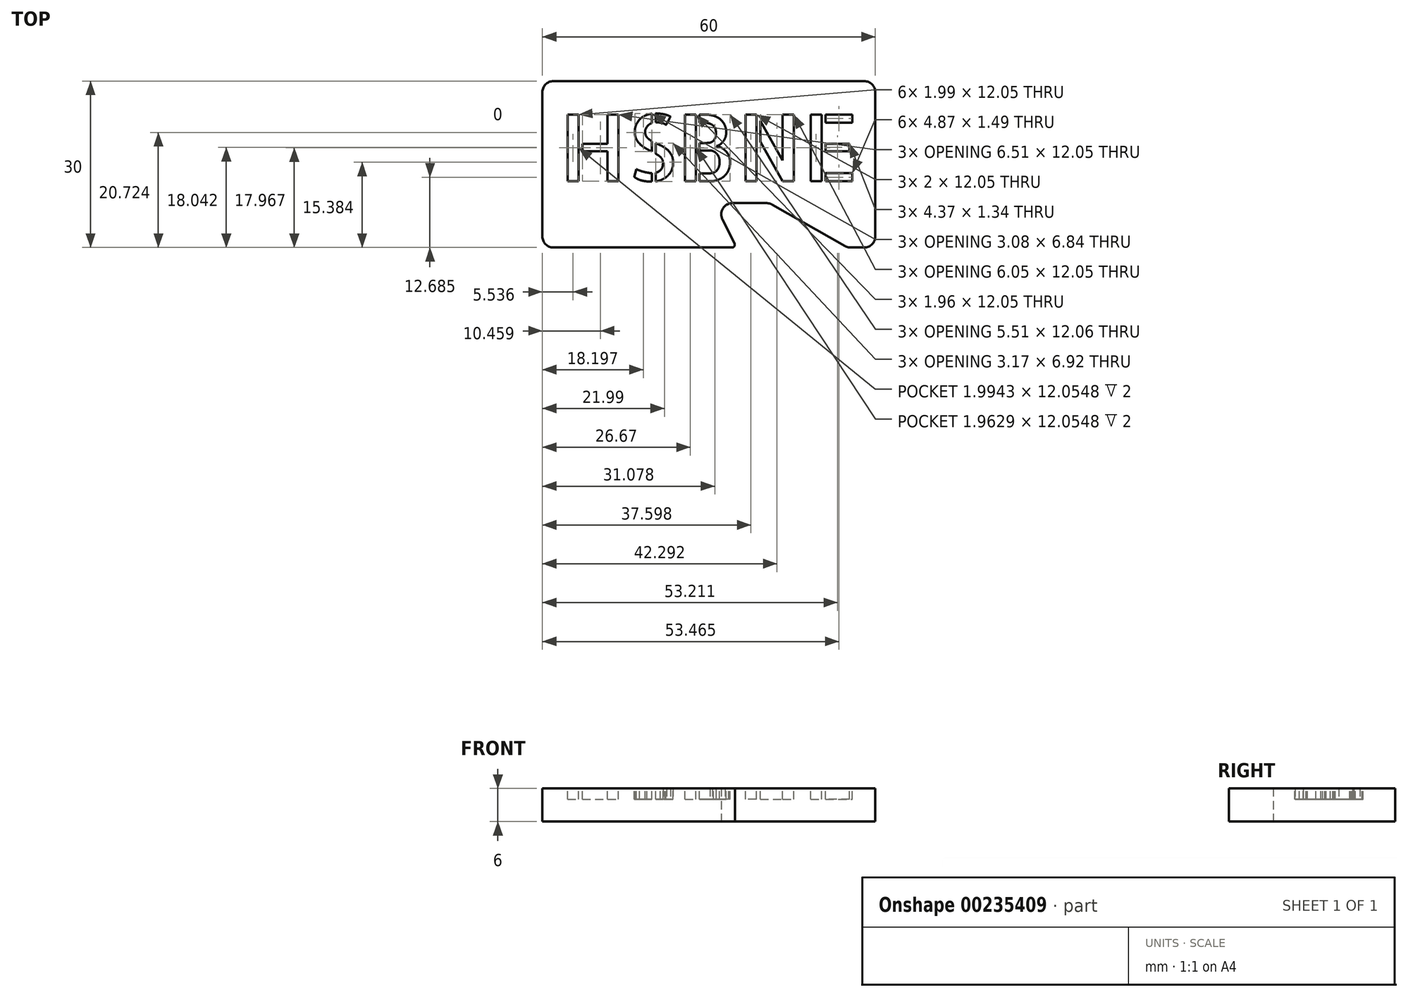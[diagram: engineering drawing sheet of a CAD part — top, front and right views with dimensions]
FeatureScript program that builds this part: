
annotation { "Feature Type Name" : "Feature", "Feature Type Description" : "" }
export const myFeature = defineFeature(function(context is Context, id is Id, definition is map)
    precondition{}
    {
        {
            var Q0;
            Q0=qCreatedBy(makeId("Top.planeOp"),FACE);
            var sketch = newSketch(context, id + "F0", { "sketchPlane" : qUnion([Q0])});
            skLineSegment(sketch, "E0", {"start": v(-28, 22) * mm, "end": v(28, 22) * mm});
            skLineSegment(sketch, "E1", {"start": v(30, 20) * mm, "end": v(30, -6) * mm});
            skLineSegment(sketch, "E2", {"start": v(28, -8) * mm, "end": v(25.53, -8) * mm});
            skLineSegment(sketch, "E3", {"start": v(24.54, -7.74) * mm, "end": v(11.46, -0.26) * mm});
            skLineSegment(sketch, "E4", {"start": v(10.47, 0) * mm, "end": v(4.24, 0) * mm});
            skLineSegment(sketch, "E5", {"start": v(2.45, -2.9) * mm, "end": v(4.64, -7.28) * mm});
            skLineSegment(sketch, "E6", {"start": v(4.2, -8) * mm, "end": v(-28, -8) * mm});
            skLineSegment(sketch, "E7", {"start": v(-30, -6) * mm, "end": v(-30, 20) * mm});
            skPoint(sketch, "E8.visualSharp", {"position": v(1, 0) * mm});
            skArc(sketch, "E8.filletArc", {"start": v(4.24, 0) * mm, "mid": v(2.53, -0.95) * mm, "end": v(2.45, -2.9) * mm});
            skPoint(sketch, "E9.visualSharp", {"position": v(11, 0) * mm});
            skArc(sketch, "E9.filletArc", {"start": v(11.46, -0.26) * mm, "mid": v(10.98, -0.07) * mm, "end": v(10.47, 0) * mm});
            skPoint(sketch, "E10.visualSharp", {"position": v(-30, -8) * mm});
            skArc(sketch, "E10.filletArc", {"start": v(-30, -6) * mm, "mid": v(-29.41, -7.41) * mm, "end": v(-28, -8) * mm});
            skPoint(sketch, "E11.visualSharp", {"position": v(-30, 22) * mm});
            skArc(sketch, "E11.filletArc", {"start": v(-28, 22) * mm, "mid": v(-29.41, 21.41) * mm, "end": v(-30, 20) * mm});
            skPoint(sketch, "E12.visualSharp", {"position": v(30, 22) * mm});
            skArc(sketch, "E12.filletArc", {"start": v(30, 20) * mm, "mid": v(29.41, 21.41) * mm, "end": v(28, 22) * mm});
            skPoint(sketch, "E13.visualSharp", {"position": v(30, -8) * mm});
            skArc(sketch, "E13.filletArc", {"start": v(28, -8) * mm, "mid": v(29.41, -7.41) * mm, "end": v(30, -6) * mm});
            skPoint(sketch, "E14.visualSharp", {"position": v(25, -8) * mm});
            skArc(sketch, "E14.filletArc", {"start": v(24.54, -7.74) * mm, "mid": v(25.02, -7.93) * mm, "end": v(25.53, -8) * mm});
            skPoint(sketch, "E15.visualSharp", {"position": v(5, -8) * mm});
            skArc(sketch, "E15.filletArc", {"start": v(4.2, -8) * mm, "mid": v(4.62, -7.76) * mm, "end": v(4.64, -7.28) * mm});
            skSolve(sketch);
        }
        {
            var Q0;
            Q0 = qSketchRegion(id + "F0", true);
            extrude(context, id + "F1", {"entities" : qUnion([Q0]), "depth" : 6 * mm});
        }
        {
            var Q0;
            Q0=makeQuery(id+"F1.opExtrude","CAP_FACE",FACE,{"disambiguationData":[OSD([sQuery(id+"F0.wireOp",EDGE,"E0"),sQuery(id+"F0.wireOp",EDGE,"E1"),sQuery(id+"F0.wireOp",EDGE,"E2"),sQuery(id+"F0.wireOp",EDGE,"E3"),sQuery(id+"F0.wireOp",EDGE,"E4"),sQuery(id+"F0.wireOp",EDGE,"E5"),sQuery(id+"F0.wireOp",EDGE,"E6"),sQuery(id+"F0.wireOp",EDGE,"E7"),sQuery(id+"F0.wireOp",EDGE,"E8.filletArc"),sQuery(id+"F0.wireOp",EDGE,"E9.filletArc"),sQuery(id+"F0.wireOp",EDGE,"E10.filletArc"),sQuery(id+"F0.wireOp",EDGE,"E11.filletArc"),sQuery(id+"F0.wireOp",EDGE,"E12.filletArc"),sQuery(id+"F0.wireOp",EDGE,"E13.filletArc"),sQuery(id+"F0.wireOp",EDGE,"E14.filletArc"),sQuery(id+"F0.wireOp",EDGE,"E15.filletArc")])],"isStart":false});
            var sketch = newSketch(context, id + "F2", { "sketchPlane" : qUnion([Q0])});
            skText(sketch, "E16", { "text": "HSBNE", "fontName": "AllertaStencil-Regular.ttf"});
            const initialGuessF2  = {"E16": [-0.027, 0.00394, 1, 0, 0.01206]};
            skSetInitialGuess(sketch, initialGuessF2);
            skSolve(sketch);
        }
        {
            var Q0;
            Q0 = qSketchRegion(id + "F2", true);
            extrude(context, id + "F3", {"entities" : qUnion([Q0]), "operationType" : NewBodyOperationType.REMOVE, "oppositeDirection" : true, "depth" : 2 * mm});
        }
    });
